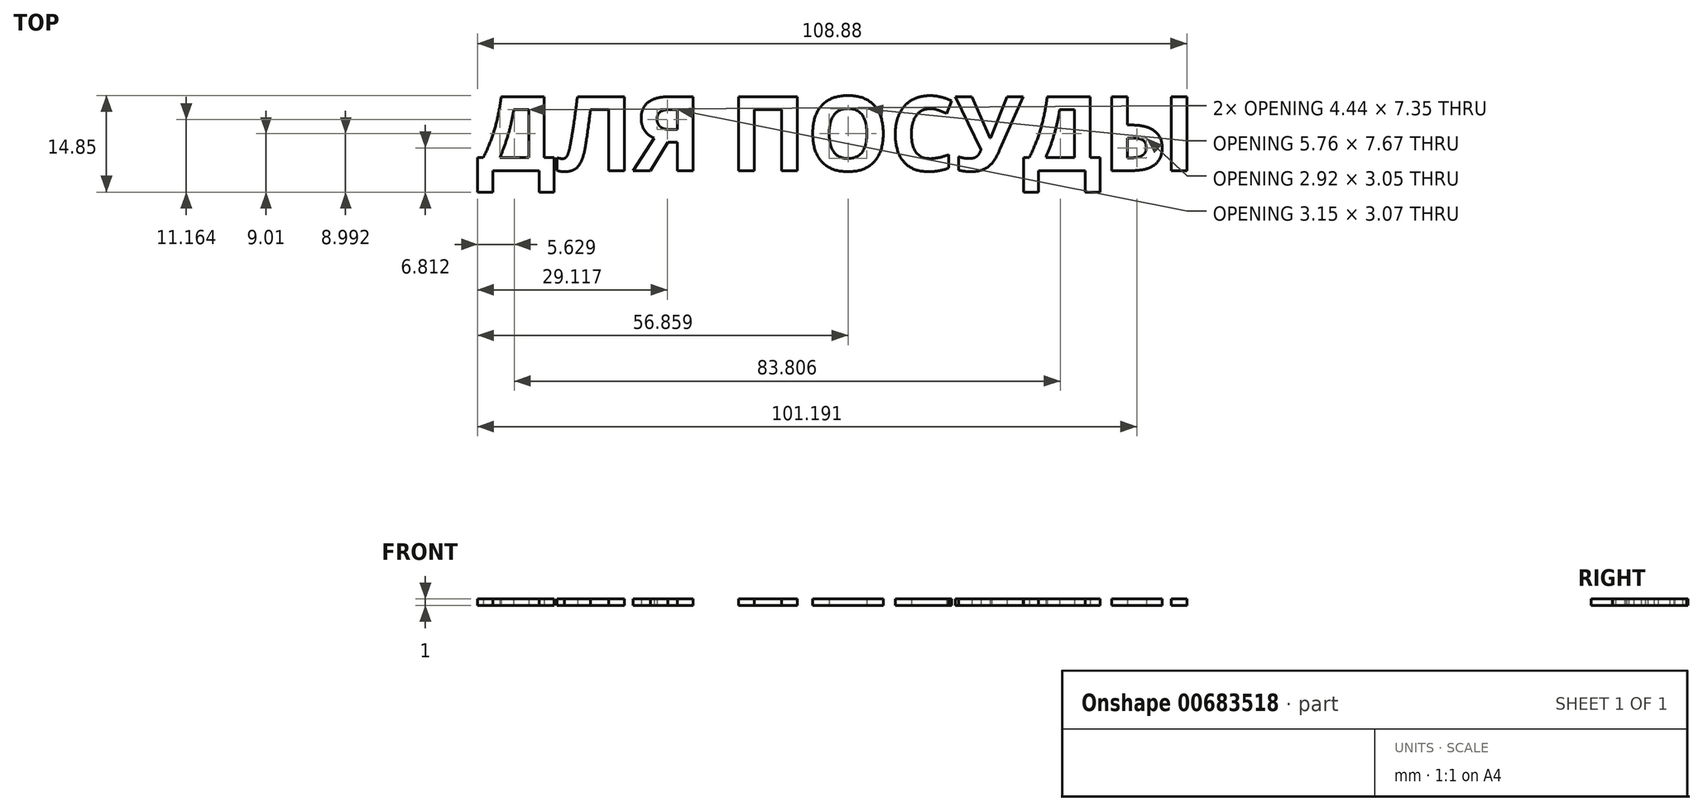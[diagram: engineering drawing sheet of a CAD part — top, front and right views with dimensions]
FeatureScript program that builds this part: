
annotation { "Feature Type Name" : "Feature", "Feature Type Description" : "" }
export const myFeature = defineFeature(function(context is Context, id is Id, definition is map)
    precondition{}
    {
        {
            var Q0;
            Q0=qCreatedBy(makeId("Top.planeOp"),FACE);
            var sketch = newSketch(context, id + "F0", { "sketchPlane" : qUnion([Q0])});
            skText(sketch, "E0", { "text": "ДЛЯ ПОСУДЫ", "fontName": "OpenSans-Bold.ttf"});
            const initialGuessF0  = {"E0": [0.0006, -0.01178, 1, 0, 0.01146]};
            skSetInitialGuess(sketch, initialGuessF0);
            skSolve(sketch);
        }
        {
            var Q0;
            Q0 = qSketchRegion(id + "F0", true);
            extrude(context, id + "F1", {"entities" : qUnion([Q0]), "depth" : 1 * mm, "offsetDistance" : 25 * mm});
        }
    });
